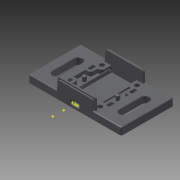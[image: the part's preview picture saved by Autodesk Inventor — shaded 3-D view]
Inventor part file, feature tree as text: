
AUTODESK INVENTOR PART (.ipt)
format: ipt  version: 2013 (Build 170138000, 138)  size: 1,174,528 bytes
history: native  units: mm (DEFAULTED — no unit token found)
features: sketch x3, plane x2, other x2, imported_body x1
ambient origin geometry x8: Origin, YZ Plane, XZ Plane, XY Plane, X Axis, Y Axis, Z Axis, Center Point
bodies: Solid1 (feature_tree)
feature tree (8):
  imported_body  "Base1"
  sketch  "Sketch1"  dims[d0=1.48938mm]
  plane  "Work Plane1"
  sketch  "Sketch2"  dims[d1=1.48938mm]
  plane  "Work Plane2"
  sketch  "Sketch3"  dims[d2=0.762mm d3=6.35mm d4=6.35mm]
  other  "Work Point4"
  other  "Work Point5"
